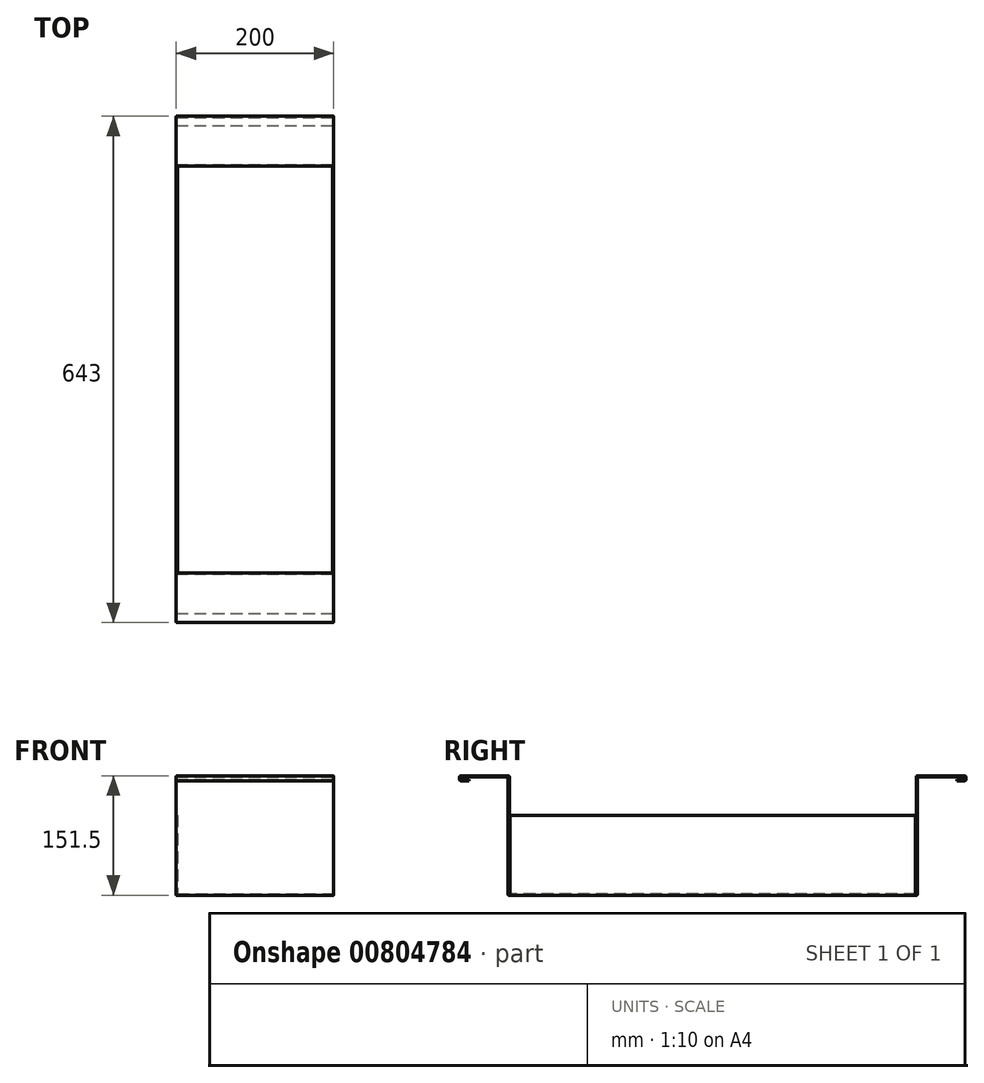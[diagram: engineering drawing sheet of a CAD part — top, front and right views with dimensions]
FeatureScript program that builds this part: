
annotation { "Feature Type Name" : "Feature", "Feature Type Description" : "" }
export const myFeature = defineFeature(function(context is Context, id is Id, definition is map)
    precondition{}
    {
        {
            var Q0;
            Q0=qCreatedBy(makeId("Right.planeOp"),FACE);
            var sketch = newSketch(context, id + "F0", { "sketchPlane" : qUnion([Q0])});
            skLineSegment(sketch, "E0", {"start": v(-304.69, 143.06) * mm, "end": v(-313.69, 143.06) * mm});
            skLineSegment(sketch, "E1", {"start": v(-314.69, 144.06) * mm, "end": v(-314.69, 145.06) * mm});
            skLineSegment(sketch, "E2", {"start": v(-313.69, 146.06) * mm, "end": v(-255.69, 146.06) * mm});
            skLineSegment(sketch, "E3", {"start": v(-254.69, 145.06) * mm, "end": v(-254.69, -2.94) * mm});
            skLineSegment(sketch, "E4", {"start": v(-253.69, -3.94) * mm, "end": v(264.31, -3.94) * mm});
            skLineSegment(sketch, "E5", {"start": v(265.31, -2.94) * mm, "end": v(265.31, 145.06) * mm});
            skLineSegment(sketch, "E6", {"start": v(266.31, 146.06) * mm, "end": v(324.31, 146.06) * mm});
            skLineSegment(sketch, "E7", {"start": v(325.31, 145.06) * mm, "end": v(325.31, 144.06) * mm});
            skLineSegment(sketch, "E8", {"start": v(324.31, 143.06) * mm, "end": v(315.31, 143.06) * mm});
            skLineSegment(sketch, "E9", {"start": v(315.31, 143.06) * mm, "end": v(315.31, 141.56) * mm});
            skLineSegment(sketch, "E10", {"start": v(315.31, 141.56) * mm, "end": v(325.81, 141.56) * mm});
            skLineSegment(sketch, "E11", {"start": v(326.81, 142.56) * mm, "end": v(326.81, 146.56) * mm});
            skLineSegment(sketch, "E12", {"start": v(325.81, 147.56) * mm, "end": v(264.81, 147.56) * mm});
            skLineSegment(sketch, "E13", {"start": v(263.81, 146.56) * mm, "end": v(263.81, -1.44) * mm});
            skLineSegment(sketch, "E14", {"start": v(262.81, -2.44) * mm, "end": v(-252.19, -2.44) * mm});
            skLineSegment(sketch, "E15", {"start": v(-253.19, -1.44) * mm, "end": v(-253.19, 146.56) * mm});
            skLineSegment(sketch, "E16", {"start": v(-254.19, 147.56) * mm, "end": v(-315.19, 147.56) * mm});
            skLineSegment(sketch, "E17", {"start": v(-316.19, 146.56) * mm, "end": v(-316.19, 142.56) * mm});
            skLineSegment(sketch, "E18", {"start": v(-315.19, 141.56) * mm, "end": v(-304.69, 141.56) * mm});
            skLineSegment(sketch, "E19", {"start": v(-304.69, 141.56) * mm, "end": v(-304.69, 143.06) * mm});
            skPoint(sketch, "E20.visualSharp", {"position": v(263.81, 147.56) * mm});
            skArc(sketch, "E20.filletArc", {"start": v(264.81, 147.56) * mm, "mid": v(264.1, 147.27) * mm, "end": v(263.81, 146.56) * mm});
            skPoint(sketch, "E21.visualSharp", {"position": v(265.31, 146.06) * mm});
            skArc(sketch, "E21.filletArc", {"start": v(266.31, 146.06) * mm, "mid": v(265.6, 145.77) * mm, "end": v(265.31, 145.06) * mm});
            skPoint(sketch, "E22.visualSharp", {"position": v(326.81, 147.56) * mm});
            skArc(sketch, "E22.filletArc", {"start": v(326.81, 146.56) * mm, "mid": v(326.52, 147.27) * mm, "end": v(325.81, 147.56) * mm});
            skPoint(sketch, "E23.visualSharp", {"position": v(325.31, 146.06) * mm});
            skArc(sketch, "E23.filletArc", {"start": v(325.31, 145.06) * mm, "mid": v(325.02, 145.77) * mm, "end": v(324.31, 146.06) * mm});
            skPoint(sketch, "E24.visualSharp", {"position": v(326.81, 141.56) * mm});
            skArc(sketch, "E24.filletArc", {"start": v(325.81, 141.56) * mm, "mid": v(326.52, 141.85) * mm, "end": v(326.81, 142.56) * mm});
            skPoint(sketch, "E25.visualSharp", {"position": v(325.31, 143.06) * mm});
            skArc(sketch, "E25.filletArc", {"start": v(324.31, 143.06) * mm, "mid": v(325.02, 143.35) * mm, "end": v(325.31, 144.06) * mm});
            skPoint(sketch, "E26.visualSharp", {"position": v(263.81, -2.44) * mm});
            skArc(sketch, "E26.filletArc", {"start": v(262.81, -2.44) * mm, "mid": v(263.52, -2.15) * mm, "end": v(263.81, -1.44) * mm});
            skPoint(sketch, "E27.visualSharp", {"position": v(265.31, -3.94) * mm});
            skArc(sketch, "E27.filletArc", {"start": v(264.31, -3.94) * mm, "mid": v(265.02, -3.65) * mm, "end": v(265.31, -2.94) * mm});
            skPoint(sketch, "E28.visualSharp", {"position": v(-253.19, -2.44) * mm});
            skArc(sketch, "E28.filletArc", {"start": v(-253.19, -1.44) * mm, "mid": v(-252.9, -2.15) * mm, "end": v(-252.19, -2.44) * mm});
            skPoint(sketch, "E29.visualSharp", {"position": v(-254.69, -3.94) * mm});
            skArc(sketch, "E29.filletArc", {"start": v(-254.69, -2.94) * mm, "mid": v(-254.4, -3.65) * mm, "end": v(-253.69, -3.94) * mm});
            skPoint(sketch, "E30.visualSharp", {"position": v(-253.19, 147.56) * mm});
            skArc(sketch, "E30.filletArc", {"start": v(-253.19, 146.56) * mm, "mid": v(-253.48, 147.27) * mm, "end": v(-254.19, 147.56) * mm});
            skPoint(sketch, "E31.visualSharp", {"position": v(-254.69, 146.06) * mm});
            skArc(sketch, "E31.filletArc", {"start": v(-254.69, 145.06) * mm, "mid": v(-254.98, 145.77) * mm, "end": v(-255.69, 146.06) * mm});
            skPoint(sketch, "E32.visualSharp", {"position": v(-316.19, 147.56) * mm});
            skArc(sketch, "E32.filletArc", {"start": v(-315.19, 147.56) * mm, "mid": v(-315.9, 147.27) * mm, "end": v(-316.19, 146.56) * mm});
            skPoint(sketch, "E33.visualSharp", {"position": v(-314.69, 146.06) * mm});
            skArc(sketch, "E33.filletArc", {"start": v(-313.69, 146.06) * mm, "mid": v(-314.4, 145.77) * mm, "end": v(-314.69, 145.06) * mm});
            skPoint(sketch, "E34.visualSharp", {"position": v(-314.69, 143.06) * mm});
            skArc(sketch, "E34.filletArc", {"start": v(-314.69, 144.06) * mm, "mid": v(-314.4, 143.35) * mm, "end": v(-313.69, 143.06) * mm});
            skPoint(sketch, "E35.visualSharp", {"position": v(-316.19, 141.56) * mm});
            skArc(sketch, "E35.filletArc", {"start": v(-316.19, 142.56) * mm, "mid": v(-315.9, 141.85) * mm, "end": v(-315.19, 141.56) * mm});
            skSolve(sketch);
        }
        {
            var Q0;
            Q0 = qSketchRegion(id + "F0", true);
            extrude(context, id + "F1", {"entities" : qUnion([Q0]), "oppositeDirection" : true, "depth" : 200 * mm, "offsetDistance" : 25 * mm});
        }
        {
            var Q0;
            Q0=makeQuery(id+"F1.opExtrude","SWEPT_FACE",FACE,{"disambiguationData":[OSD([sQuery(id+"F0.wireOp",EDGE,"E14")])]});
            var sketch = newSketch(context, id + "F2", { "sketchPlane" : qUnion([Q0])});
            skLineSegment(sketch, "E36.bottom", {"start": v(0, 262.81) * mm, "end": v(-1.5, 262.81) * mm});
            skLineSegment(sketch, "E36.top", {"start": v(0, -252.19) * mm, "end": v(-1.5, -252.19) * mm});
            skLineSegment(sketch, "E36.left", {"start": v(0, 262.81) * mm, "end": v(0, -252.19) * mm});
            skLineSegment(sketch, "E36.right", {"start": v(-1.5, 262.81) * mm, "end": v(-1.5, -252.19) * mm});
            skLineSegment(sketch, "E37.bottom", {"start": v(-200, 262.81) * mm, "end": v(-198.5, 262.81) * mm});
            skLineSegment(sketch, "E37.top", {"start": v(-200, -252.19) * mm, "end": v(-198.5, -252.19) * mm});
            skLineSegment(sketch, "E37.left", {"start": v(-200, 262.81) * mm, "end": v(-200, -252.19) * mm});
            skLineSegment(sketch, "E37.right", {"start": v(-198.5, 262.81) * mm, "end": v(-198.5, -252.19) * mm});
            skSolve(sketch);
        }
        {
            var Q0;
            Q0 = qSketchRegion(id + "F2", true);
            extrude(context, id + "F3", {"entities" : qUnion([Q0]), "operationType" : NewBodyOperationType.ADD, "depth" : 100 * mm, "offsetDistance" : 25 * mm});
        }
    });
